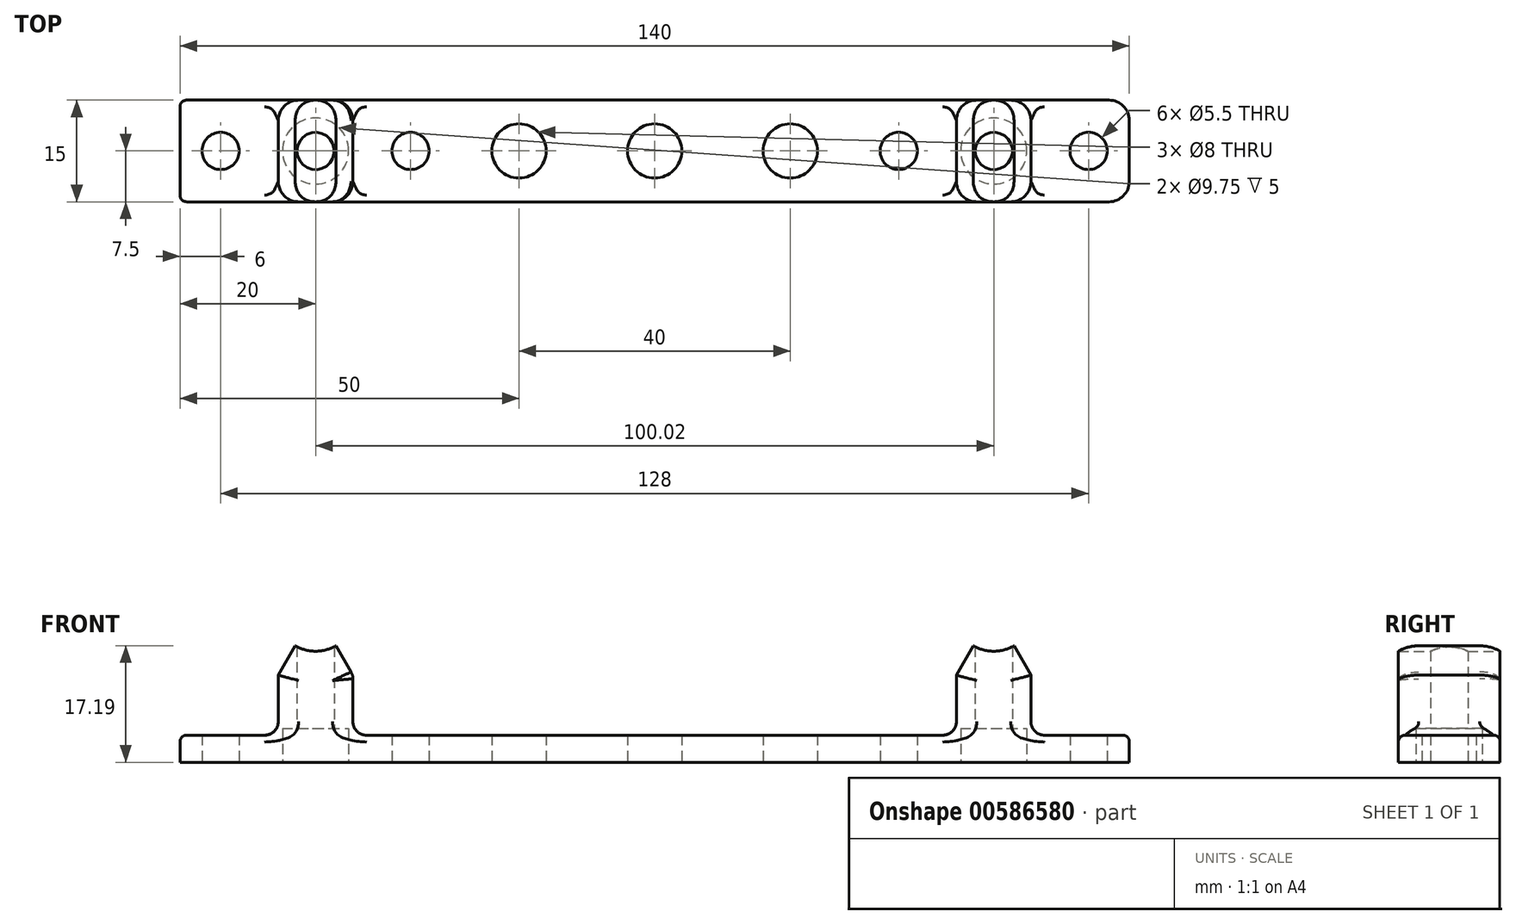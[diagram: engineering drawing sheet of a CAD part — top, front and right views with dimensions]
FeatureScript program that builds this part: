
annotation { "Feature Type Name" : "Feature", "Feature Type Description" : "" }
export const myFeature = defineFeature(function(context is Context, id is Id, definition is map)
    precondition{}
    {
        {
            var Q0;
            Q0=qCreatedBy(makeId("Front.planeOp"),FACE);
            var sketch = newSketch(context, id + "F0", { "sketchPlane" : qUnion([Q0])});
            skArc(sketch, "E0", {"start": v(-3, 17.2) * mm, "mid": v(0, 16.4) * mm, "end": v(3, 17.2) * mm});
            skLineSegment(sketch, "E1", {"start": v(3, 17.2) * mm, "end": v(5.5, 12.86) * mm});
            skLineSegment(sketch, "E2", {"start": v(-20, 0) * mm, "end": v(-20, 4) * mm});
            skLineSegment(sketch, "E3", {"start": v(-20, 4) * mm, "end": v(-5.5, 4) * mm});
            skLineSegment(sketch, "E4", {"start": v(-3, 17.2) * mm, "end": v(-5.5, 12.86) * mm});
            skLineSegment(sketch, "E5", {"start": v(5.5, 4) * mm, "end": v(5.5, 12.86) * mm});
            skLineSegment(sketch, "E6", {"start": v(-5.5, 4) * mm, "end": v(-5.5, 12.86) * mm});
            skLineSegment(sketch, "E7", {"start": v(120, 0) * mm, "end": v(120, 4) * mm});
            skArc(sketch, "E8", {"start": v(97, 17.2) * mm, "mid": v(100, 16.4) * mm, "end": v(103, 17.2) * mm});
            skLineSegment(sketch, "E9", {"start": v(103, 17.2) * mm, "end": v(105.5, 12.86) * mm});
            skLineSegment(sketch, "E10", {"start": v(97, 17.2) * mm, "end": v(94.5, 12.86) * mm});
            skLineSegment(sketch, "E11", {"start": v(105.5, 4) * mm, "end": v(105.5, 12.86) * mm});
            skLineSegment(sketch, "E12", {"start": v(94.5, 4) * mm, "end": v(94.5, 12.86) * mm});
            skLineSegment(sketch, "E13", {"start": v(120, 4) * mm, "end": v(105.5, 4) * mm});
            skLineSegment(sketch, "E14", {"start": v(94.5, 4) * mm, "end": v(5.5, 4) * mm});
            skLineSegment(sketch, "E15", {"start": v(-20, 0) * mm, "end": v(120, 0) * mm});
            skSolve(sketch);
        }
        {
            var Q0;
            Q0=makeQuery(id+"F0.imprint","IMPRINT",FACE,{"disambiguationData":[TD([[makeQuery(id+"F0.imprint","IMPRINT",EDGE,{"derivedFrom":sQuery(id+"F0.wireOp",EDGE,"E0")}),-1.0]])]});
            extrude(context, id + "F1", {"entities" : qUnion([Q0]), "endBound" : BoundingType.SYMMETRIC, "depth" : 15 * mm, "offsetDistance" : 25 * mm});
        }
        {
            var Q0;
            Q0=makeQuery(id+"F1.opExtrude","SWEPT_FACE",FACE,{"disambiguationData":[OSD([sQuery(id+"F0.wireOp",EDGE,"E15")])]});
            var sketch = newSketch(context, id + "F2", { "sketchPlane" : qUnion([Q0])});
            skPoint(sketch, "E16.endSnap0", {"position": v(-25.36, 0) * mm});
            skCircle(sketch, "E17", {"center": v(0, 0) * mm, "radius": 1.92 * mm});
            skCircle(sketch, "E18", {"center": v(-14, 0) * mm, "radius": 2.73 * mm});
            skCircle(sketch, "E19", {"center": v(14, 0) * mm, "radius": 2.8 * mm});
            skCircle(sketch, "E20", {"center": v(114, 0) * mm, "radius": 2.21 * mm});
            skCircle(sketch, "E21", {"center": v(100.02, 0) * mm, "radius": 2.05 * mm});
            skCircle(sketch, "E22", {"center": v(86, 0) * mm, "radius": 2.81 * mm});
            skCircle(sketch, "E23", {"center": v(50, 0) * mm, "radius": 4.56 * mm});
            skCircle(sketch, "E24", {"center": v(70, 0) * mm, "radius": 3.53 * mm});
            skCircle(sketch, "E25", {"center": v(30, 0) * mm, "radius": 3.75 * mm});
            skSolve(sketch);
        }
        {
            var Q0;
            Q0=sQuery(id+"F2.wireOp",VERTEX,"hxb4wzW3-ZKgS-2oYC-36ei-CTC3hNMR9Hjz.center");
            var Q1;
            Q1=sQuery(id+"F2.wireOp",VERTEX,"E17.center");
            var Q2;
            Q2=sQuery(id+"F2.wireOp",VERTEX,"E21.center");
            var Q3;
            Q3=makeQuery(id+"F1.opExtrude","SWEPT_BODY",BODY,{"disambiguationData":[OSD([sQuery(id+"F0.wireOp",EDGE,"zX9CnGYi-FHMu-CDTd-3qtW-jb8D0Be0Aeue"),sQuery(id+"F0.wireOp",EDGE,"uUa6HIWN-VWHU-dLsz-Tg3L-AYrsauEqXgol"),sQuery(id+"F0.wireOp",EDGE,"E0"),sQuery(id+"F0.wireOp",EDGE,"E1"),sQuery(id+"F0.wireOp",EDGE,"KlZl9Qz2-CevD-vnXL-ENTq-fczEF3EJsqGr"),sQuery(id+"F0.wireOp",EDGE,"E2"),sQuery(id+"F0.wireOp",EDGE,"E3"),sQuery(id+"F0.wireOp",EDGE,"E4"),sQuery(id+"F0.wireOp",EDGE,"7b223aeb-5d7b-4c51-ac3c-0f3b1bb038bc.trimOffspring"),sQuery(id+"F0.wireOp",EDGE,"E5"),sQuery(id+"F0.wireOp",EDGE,"E6")])]});
            hole(context, id + "F3", {"style" : HoleStyle.C_BORE, "endStyle" : HoleEndStyle.THROUGH, "standardTappedOrClearance" : lookupTablePath({ "standard" : "ISO", "fit" : "Normal", "size" : "M5", "type" : "Clearance" }), "standardBlindInLast" : lookupTablePath({ "fit" : "Standard", "standard" : "ISO", "size" : "M5", "type" : "Clearance" }), "holeDiameter" : 5.5 * mm, "cBoreDiameter" : 9.75 * mm, "cBoreDepth" : 5 * mm, "majorDiameter" : 5 * mm, "isTappedThrough" : true, "tappedDepth" : 12 * mm, "tapClearance" : 3, "startFromSketch" : true, "locations" : qUnion([Q0, Q1, Q2]), "scope" : qUnion([Q3])});
        }
        {
            var Q0;
            Q0=sQuery(id+"F2.wireOp",VERTEX,"ay5H3own-NBzd-g8TW-vI32-CYLiJ3faHReW.end");
            var Q1;
            Q1=sQuery(id+"F2.wireOp",VERTEX,"WPoO8dip-KUI3-5gfj-09B3-eG0CMI9dBefV.center");
            var Q2;
            Q2=sQuery(id+"F2.wireOp",VERTEX,"E18.center");
            var Q3;
            Q3=sQuery(id+"F2.wireOp",VERTEX,"E19.center");
            var Q4;
            Q4=sQuery(id+"F2.wireOp",VERTEX,"E22.center");
            var Q5;
            Q5=sQuery(id+"F2.wireOp",VERTEX,"E20.center");
            var Q6;
            Q6=makeQuery(id+"F1.opExtrude","SWEPT_BODY",BODY,{"disambiguationData":[OSD([sQuery(id+"F0.wireOp",EDGE,"zX9CnGYi-FHMu-CDTd-3qtW-jb8D0Be0Aeue"),sQuery(id+"F0.wireOp",EDGE,"uUa6HIWN-VWHU-dLsz-Tg3L-AYrsauEqXgol"),sQuery(id+"F0.wireOp",EDGE,"E0"),sQuery(id+"F0.wireOp",EDGE,"E1"),sQuery(id+"F0.wireOp",EDGE,"KlZl9Qz2-CevD-vnXL-ENTq-fczEF3EJsqGr"),sQuery(id+"F0.wireOp",EDGE,"E2"),sQuery(id+"F0.wireOp",EDGE,"E3"),sQuery(id+"F0.wireOp",EDGE,"E4"),sQuery(id+"F0.wireOp",EDGE,"7b223aeb-5d7b-4c51-ac3c-0f3b1bb038bc.trimOffspring"),sQuery(id+"F0.wireOp",EDGE,"E5"),sQuery(id+"F0.wireOp",EDGE,"E6")])]});
            hole(context, id + "F4", {"style" : HoleStyle.SIMPLE, "endStyle" : HoleEndStyle.THROUGH, "holeDiameter" : 5.5 * mm, "majorDiameter" : 5 * mm, "isTappedThrough" : true, "tappedDepth" : 12 * mm, "tapClearance" : 3, "startFromSketch" : true, "locations" : qUnion([Q0, Q1, Q2, Q3, Q4, Q5]), "scope" : qUnion([Q6])});
        }
        {
            var Q0;
            Q0=makeQuery(id+"F1.opExtrude","CAP_EDGE",EDGE,{"disambiguationData":[OSD([sQuery(id+"F0.wireOp",EDGE,"uUa6HIWN-VWHU-dLsz-Tg3L-AYrsauEqXgol")])],"isStart":false});
            var Q1;
            Q1=makeQuery(id+"F1.opExtrude","CAP_EDGE",EDGE,{"disambiguationData":[OSD([sQuery(id+"F0.wireOp",EDGE,"E2")])],"isStart":true});
            var Q2;
            Q2=makeQuery(id+"F1.opExtrude","CAP_EDGE",EDGE,{"disambiguationData":[OSD([sQuery(id+"F0.wireOp",EDGE,"E2")])],"isStart":false});
            var Q3;
            Q3=makeQuery(id+"F1.opExtrude","CAP_EDGE",EDGE,{"disambiguationData":[OSD([sQuery(id+"F0.wireOp",EDGE,"E3")])],"isStart":false});
            var Q4;
            Q4=makeQuery(id+"F1.opExtrude","SWEPT_EDGE",EDGE,{"disambiguationData":[OSD([sQuery(id+"F0.wireOp",EDGE,"E2"),sQuery(id+"F0.wireOp",EDGE,"E3")])]});
            var Q5;
            Q5=makeQuery(id+"F1.opExtrude","CAP_EDGE",EDGE,{"disambiguationData":[OSD([sQuery(id+"F0.wireOp",EDGE,"E3")])],"isStart":true});
            var Q6;
            Q6=makeQuery(id+"F1.opExtrude","CAP_EDGE",EDGE,{"disambiguationData":[OSD([sQuery(id+"F0.wireOp",EDGE,"7b223aeb-5d7b-4c51-ac3c-0f3b1bb038bc.trimOffspring")])],"isStart":false});
            var Q7;
            Q7=makeQuery(id+"F1.opExtrude","SWEPT_EDGE",EDGE,{"disambiguationData":[OSD([sQuery(id+"F0.wireOp",EDGE,"uUa6HIWN-VWHU-dLsz-Tg3L-AYrsauEqXgol"),sQuery(id+"F0.wireOp",EDGE,"7b223aeb-5d7b-4c51-ac3c-0f3b1bb038bc.trimOffspring")])]});
            var Q8;
            Q8=makeQuery(id+"F1.opExtrude","CAP_EDGE",EDGE,{"disambiguationData":[OSD([sQuery(id+"F0.wireOp",EDGE,"7b223aeb-5d7b-4c51-ac3c-0f3b1bb038bc.trimOffspring")])],"isStart":true});
            var Q9;
            Q9=makeQuery(id+"F1.opExtrude","CAP_EDGE",EDGE,{"disambiguationData":[OSD([sQuery(id+"F0.wireOp",EDGE,"E14")])],"isStart":false});
            var Q10;
            Q10=makeQuery(id+"F1.opExtrude","CAP_EDGE",EDGE,{"disambiguationData":[OSD([sQuery(id+"F0.wireOp",EDGE,"E13")])],"isStart":false});
            var Q11;
            Q11=makeQuery(id+"F1.opExtrude","SWEPT_EDGE",EDGE,{"disambiguationData":[OSD([sQuery(id+"F0.wireOp",EDGE,"E7"),sQuery(id+"F0.wireOp",EDGE,"E13")])]});
            var Q12;
            Q12=makeQuery(id+"F1.opExtrude","CAP_EDGE",EDGE,{"disambiguationData":[OSD([sQuery(id+"F0.wireOp",EDGE,"E14")])],"isStart":true});
            var Q13;
            Q13=makeQuery(id+"F1.opExtrude","CAP_EDGE",EDGE,{"disambiguationData":[OSD([sQuery(id+"F0.wireOp",EDGE,"E13")])],"isStart":true});
            fillet(context, id + "F5", {"entities" : qUnion([Q0, Q1, Q2, Q3, Q4, Q5, Q6, Q7, Q8, Q9, Q10, Q11, Q12, Q13]), "radius" : 1 * mm, "tangentPropagation" : true, "allowEdgeOverflow" : false});
        }
        {
            var Q0;
            Q0=makeQuery(id+"F1.opExtrude","SWEPT_EDGE",EDGE,{"disambiguationData":[OSD([sQuery(id+"F0.wireOp",EDGE,"E3"),sQuery(id+"F0.wireOp",EDGE,"E6")])]});
            var Q1;
            Q1=makeQuery(id+"F1.opExtrude","SWEPT_EDGE",EDGE,{"disambiguationData":[OSD([sQuery(id+"F0.wireOp",EDGE,"7b223aeb-5d7b-4c51-ac3c-0f3b1bb038bc.trimOffspring"),sQuery(id+"F0.wireOp",EDGE,"E5")])]});
            var Q2;
            Q2=makeQuery(id+"F1.opExtrude","SWEPT_EDGE",EDGE,{"disambiguationData":[OSD([sQuery(id+"F0.wireOp",EDGE,"E11"),sQuery(id+"F0.wireOp",EDGE,"E13")])]});
            var Q3;
            Q3=makeQuery(id+"F1.opExtrude","SWEPT_EDGE",EDGE,{"disambiguationData":[OSD([sQuery(id+"F0.wireOp",EDGE,"E12"),sQuery(id+"F0.wireOp",EDGE,"E14")])]});
            fillet(context, id + "F6", {"entities" : qUnion([Q0, Q1, Q2, Q3]), "radius" : 2 * mm, "tangentPropagation" : true, "allowEdgeOverflow" : false});
        }
        {
            var Q0;
            Q0=makeQuery(id+"F1.opExtrude","CAP_EDGE",EDGE,{"disambiguationData":[OSD([sQuery(id+"F0.wireOp",EDGE,"E6")])],"isStart":false});
            var Q1;
            Q1=makeQuery(id+"F1.opExtrude","CAP_EDGE",EDGE,{"disambiguationData":[OSD([sQuery(id+"F0.wireOp",EDGE,"E5")])],"isStart":false});
            var Q2;
            Q2=makeQuery(id+"F1.opExtrude","CAP_EDGE",EDGE,{"disambiguationData":[OSD([sQuery(id+"F0.wireOp",EDGE,"E12")])],"isStart":false});
            var Q3;
            Q3=makeQuery(id+"F1.opExtrude","CAP_EDGE",EDGE,{"disambiguationData":[OSD([sQuery(id+"F0.wireOp",EDGE,"E11")])],"isStart":false});
            var Q4;
            Q4=makeQuery(id+"F1.opExtrude","CAP_EDGE",EDGE,{"disambiguationData":[OSD([sQuery(id+"F0.wireOp",EDGE,"E11")])],"isStart":true});
            var Q5;
            Q5=makeQuery(id+"F1.opExtrude","CAP_EDGE",EDGE,{"disambiguationData":[OSD([sQuery(id+"F0.wireOp",EDGE,"E12")])],"isStart":true});
            var Q6;
            Q6=makeQuery(id+"F1.opExtrude","CAP_EDGE",EDGE,{"disambiguationData":[OSD([sQuery(id+"F0.wireOp",EDGE,"E6")])],"isStart":true});
            var Q7;
            Q7=makeQuery(id+"F1.opExtrude","CAP_EDGE",EDGE,{"disambiguationData":[OSD([sQuery(id+"F0.wireOp",EDGE,"E5")])],"isStart":true});
            var Q8;
            Q8=makeQuery(id+"F1.opExtrude","CAP_EDGE",EDGE,{"disambiguationData":[OSD([sQuery(id+"F0.wireOp",EDGE,"E4")])],"isStart":true});
            var Q9;
            Q9=makeQuery(id+"F1.opExtrude","CAP_EDGE",EDGE,{"disambiguationData":[OSD([sQuery(id+"F0.wireOp",EDGE,"E9")])],"isStart":true});
            var Q10;
            Q10=makeQuery(id+"F1.opExtrude","CAP_EDGE",EDGE,{"disambiguationData":[OSD([sQuery(id+"F0.wireOp",EDGE,"E10")])],"isStart":true});
            var Q11;
            Q11=makeQuery(id+"F1.opExtrude","CAP_EDGE",EDGE,{"disambiguationData":[OSD([sQuery(id+"F0.wireOp",EDGE,"E9")])],"isStart":false});
            var Q12;
            Q12=makeQuery(id+"F1.opExtrude","CAP_EDGE",EDGE,{"disambiguationData":[OSD([sQuery(id+"F0.wireOp",EDGE,"E4")])],"isStart":false});
            var Q13;
            Q13=makeQuery(id+"F1.opExtrude","CAP_EDGE",EDGE,{"disambiguationData":[OSD([sQuery(id+"F0.wireOp",EDGE,"E10")])],"isStart":false});
            var Q14;
            Q14=makeQuery(id+"F1.opExtrude","CAP_EDGE",EDGE,{"disambiguationData":[OSD([sQuery(id+"F0.wireOp",EDGE,"E7")])],"isStart":true});
            var Q15;
            Q15=makeQuery(id+"F1.opExtrude","CAP_EDGE",EDGE,{"disambiguationData":[OSD([sQuery(id+"F0.wireOp",EDGE,"E7")])],"isStart":false});
            fillet(context, id + "F7", {"entities" : qUnion([Q0, Q1, Q2, Q3, Q4, Q5, Q6, Q7, Q8, Q9, Q10, Q11, Q12, Q13, Q14, Q15]), "radius" : 3 * mm, "tangentPropagation" : true, "allowEdgeOverflow" : false});
        }
        {
            var Q0;
            Q0=sQuery(id+"F2.wireOp",VERTEX,"E25.center");
            var Q1;
            Q1=sQuery(id+"F2.wireOp",VERTEX,"E23.center");
            var Q2;
            Q2=sQuery(id+"F2.wireOp",VERTEX,"E24.center");
            var Q3;
            Q3=makeQuery(id+"F1.opExtrude","SWEPT_BODY",BODY,{"disambiguationData":[OSD([sQuery(id+"F0.wireOp",EDGE,"E0"),sQuery(id+"F0.wireOp",EDGE,"E1"),sQuery(id+"F0.wireOp",EDGE,"E2"),sQuery(id+"F0.wireOp",EDGE,"E3"),sQuery(id+"F0.wireOp",EDGE,"E4"),sQuery(id+"F0.wireOp",EDGE,"E5"),sQuery(id+"F0.wireOp",EDGE,"E6"),sQuery(id+"F0.wireOp",EDGE,"E7"),sQuery(id+"F0.wireOp",EDGE,"E8"),sQuery(id+"F0.wireOp",EDGE,"E9"),sQuery(id+"F0.wireOp",EDGE,"E10"),sQuery(id+"F0.wireOp",EDGE,"E11"),sQuery(id+"F0.wireOp",EDGE,"E12"),sQuery(id+"F0.wireOp",EDGE,"E13"),sQuery(id+"F0.wireOp",EDGE,"E14"),sQuery(id+"F0.wireOp",EDGE,"E15")])]});
            hole(context, id + "F8", {"style" : HoleStyle.SIMPLE, "endStyle" : HoleEndStyle.THROUGH, "holeDiameter" : 8 * mm, "majorDiameter" : 5 * mm, "isTappedThrough" : true, "tappedDepth" : 12 * mm, "tapClearance" : 3, "startFromSketch" : true, "locations" : qUnion([Q0, Q1, Q2]), "scope" : qUnion([Q3])});
        }
    });
